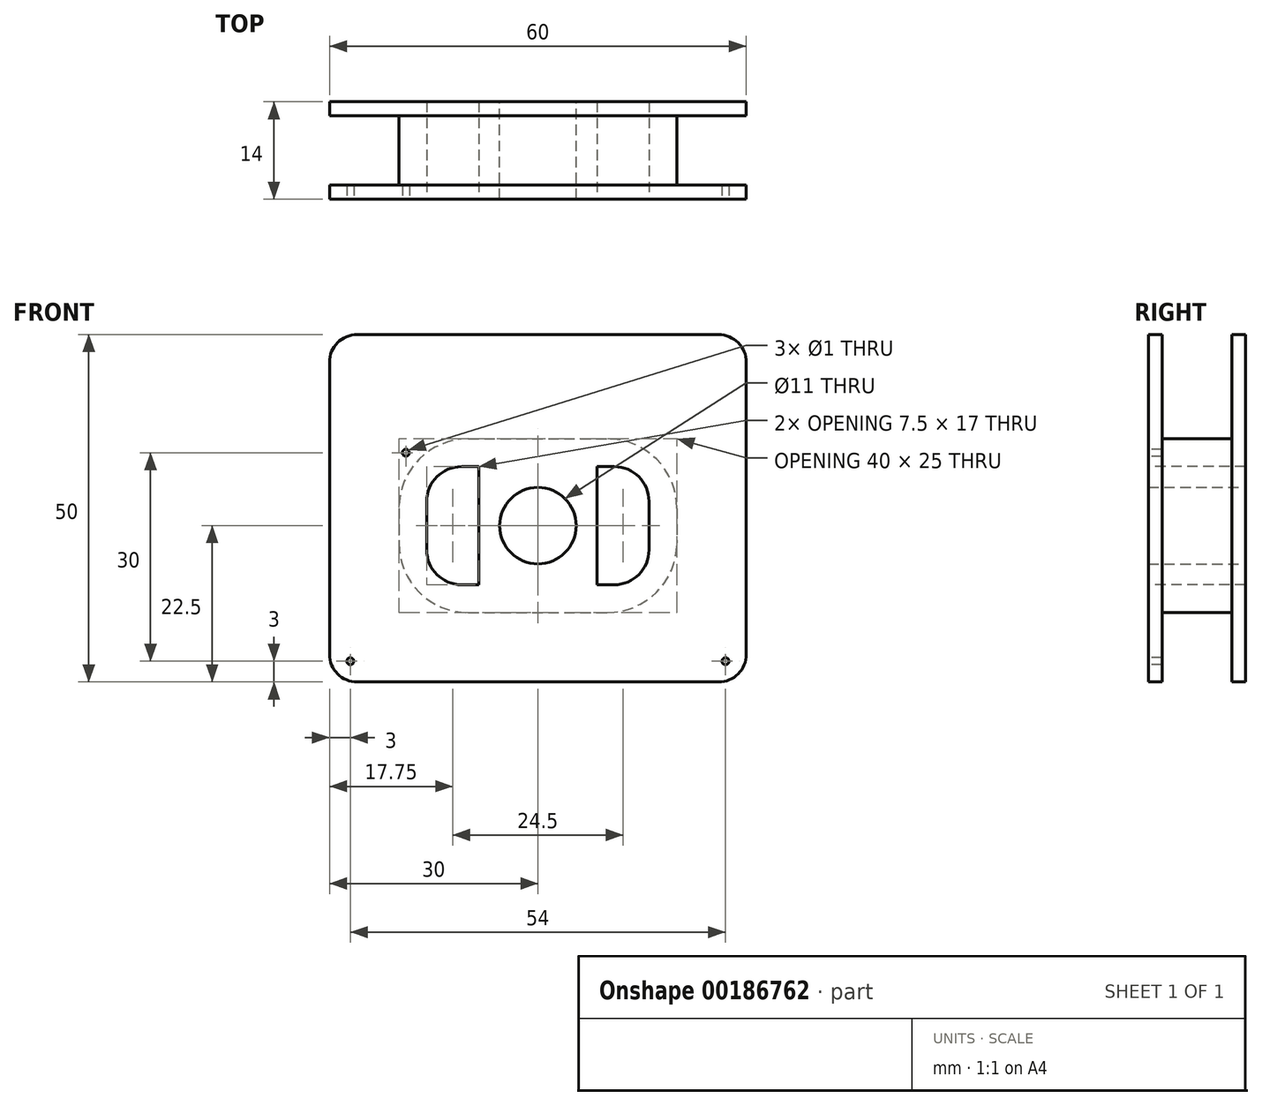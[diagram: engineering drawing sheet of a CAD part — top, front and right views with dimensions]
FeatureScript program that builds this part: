
annotation { "Feature Type Name" : "Feature", "Feature Type Description" : "" }
export const myFeature = defineFeature(function(context is Context, id is Id, definition is map)
    precondition{}
    {
        {
            var Q0;
            Q0=qCreatedBy(makeId("Front.planeOp"),FACE);
            var sketch = newSketch(context, id + "F0", { "sketchPlane" : qUnion([Q0])});
            skLineSegment(sketch, "E0.bottom", {"start": v(30, -22.5) * mm, "end": v(-30, -22.5) * mm});
            skLineSegment(sketch, "E0.top", {"start": v(30, 27.5) * mm, "end": v(-30, 27.5) * mm});
            skLineSegment(sketch, "E0.left", {"start": v(30, -22.5) * mm, "end": v(30, 27.5) * mm});
            skLineSegment(sketch, "E0.right", {"start": v(-30, -22.5) * mm, "end": v(-30, 27.5) * mm});
            skCircle(sketch, "E1", {"center": v(0, 0) * mm, "radius": 5.5 * mm});
            skSolve(sketch);
        }
        {
            var Q0;
            Q0=qSketchRegion(id+"F0",true);
            extrude(context, id + "F1", {"entities" : qUnion([Q0]), "depth" : 2 * mm});
        }
        {
            var Q0;
            Q0=makeQuery(id+"F1.opExtrude","CAP_FACE",FACE,{"disambiguationData":[OSD([sQuery(id+"F0.wireOp",EDGE,"E0.bottom"),sQuery(id+"F0.wireOp",EDGE,"E0.top"),sQuery(id+"F0.wireOp",EDGE,"E0.left"),sQuery(id+"F0.wireOp",EDGE,"E0.right"),sQuery(id+"F0.wireOp",EDGE,"E1")])],"isStart":false});
            var sketch = newSketch(context, id + "F2", { "sketchPlane" : qUnion([Q0])});
            skLineSegment(sketch, "E2.bottom", {"start": v(-20, 12.5) * mm, "end": v(20, 12.5) * mm});
            skLineSegment(sketch, "E2.top", {"start": v(-20, -12.5) * mm, "end": v(20, -12.5) * mm});
            skLineSegment(sketch, "E2.left", {"start": v(-20, 12.5) * mm, "end": v(-20, -12.5) * mm});
            skLineSegment(sketch, "E2.right", {"start": v(20, 12.5) * mm, "end": v(20, -12.5) * mm});
            skPoint(sketch, "E2.middle", {"position": v(0, 0) * mm});
            skCircle(sketch, "E3", {"center": v(0, 0) * mm, "radius": 5.5 * mm});
            skSolve(sketch);
        }
        {
            var Q0;
            Q0=qSketchRegion(id+"F2",true);
            extrude(context, id + "F3", {"entities" : qUnion([Q0]), "operationType" : NewBodyOperationType.ADD, "depth" : 10 * mm});
        }
        {
            var Q0;
            Q0=makeQuery(id+"F3.opExtrude","SWEPT_EDGE",EDGE,{"disambiguationData":[OSD([sQuery(id+"F2.wireOp",EDGE,"E2.bottom"),sQuery(id+"F2.wireOp",EDGE,"E2.right")])]});
            var Q1;
            Q1=makeQuery(id+"F3.opExtrude","SWEPT_EDGE",EDGE,{"disambiguationData":[OSD([sQuery(id+"F2.wireOp",EDGE,"E2.top"),sQuery(id+"F2.wireOp",EDGE,"E2.right")])]});
            var Q2;
            Q2=makeQuery(id+"F3.opExtrude","SWEPT_EDGE",EDGE,{"disambiguationData":[OSD([sQuery(id+"F2.wireOp",EDGE,"E2.top"),sQuery(id+"F2.wireOp",EDGE,"E2.left")])]});
            var Q3;
            Q3=makeQuery(id+"F3.opExtrude","SWEPT_EDGE",EDGE,{"disambiguationData":[OSD([sQuery(id+"F2.wireOp",EDGE,"E2.bottom"),sQuery(id+"F2.wireOp",EDGE,"E2.left")])]});
            fillet(context, id + "F4", {"entities" : qUnion([Q0, Q1, Q2, Q3]), "radius" : 10 * mm, "tangentPropagation" : true, "allowEdgeOverflow" : false});
        }
        {
            var Q0;
            Q0=makeQuery(id+"F3.opExtrude","CAP_FACE",FACE,{"disambiguationData":[OSD([sQuery(id+"F2.wireOp",EDGE,"E2.bottom"),sQuery(id+"F2.wireOp",EDGE,"E2.top"),sQuery(id+"F2.wireOp",EDGE,"E2.left"),sQuery(id+"F2.wireOp",EDGE,"E2.right"),sQuery(id+"F2.wireOp",EDGE,"E3")])],"isStart":false});
            var sketch = newSketch(context, id + "F5", { "sketchPlane" : qUnion([Q0])});
            skLineSegment(sketch, "E4.bottom", {"start": v(-30, -22.5) * mm, "end": v(30, -22.5) * mm});
            skLineSegment(sketch, "E4.top", {"start": v(-30, 27.5) * mm, "end": v(30, 27.5) * mm});
            skLineSegment(sketch, "E4.left", {"start": v(-30, -22.5) * mm, "end": v(-30, 27.5) * mm});
            skLineSegment(sketch, "E4.right", {"start": v(30, -22.5) * mm, "end": v(30, 27.5) * mm});
            skCircle(sketch, "E5", {"center": v(0, 0) * mm, "radius": 5.5 * mm});
            skSolve(sketch);
        }
        {
            var Q0;
            Q0=qSketchRegion(id+"F5",true);
            extrude(context, id + "F6", {"entities" : qUnion([Q0]), "operationType" : NewBodyOperationType.ADD, "depth" : 2 * mm});
        }
        {
            var Q0;
            Q0=makeQuery(id+"F6.opExtrude","SWEPT_EDGE",EDGE,{"disambiguationData":[OSD([sQuery(id+"F5.wireOp",EDGE,"E4.top"),sQuery(id+"F5.wireOp",EDGE,"E4.right")])]});
            var Q1;
            Q1=makeQuery(id+"F1.opExtrude","SWEPT_EDGE",EDGE,{"disambiguationData":[OSD([sQuery(id+"F0.wireOp",EDGE,"E0.top"),sQuery(id+"F0.wireOp",EDGE,"E0.left")])]});
            var Q2;
            Q2=makeQuery(id+"F6.opExtrude","SWEPT_EDGE",EDGE,{"disambiguationData":[OSD([sQuery(id+"F5.wireOp",EDGE,"E4.bottom"),sQuery(id+"F5.wireOp",EDGE,"E4.right")])]});
            var Q3;
            Q3=makeQuery(id+"F1.opExtrude","SWEPT_EDGE",EDGE,{"disambiguationData":[OSD([sQuery(id+"F0.wireOp",EDGE,"E0.bottom"),sQuery(id+"F0.wireOp",EDGE,"E0.left")])]});
            var Q4;
            Q4=makeQuery(id+"F6.opExtrude","SWEPT_EDGE",EDGE,{"disambiguationData":[OSD([sQuery(id+"F5.wireOp",EDGE,"E4.bottom"),sQuery(id+"F5.wireOp",EDGE,"E4.left")])]});
            var Q5;
            Q5=makeQuery(id+"F1.opExtrude","SWEPT_EDGE",EDGE,{"disambiguationData":[OSD([sQuery(id+"F0.wireOp",EDGE,"E0.bottom"),sQuery(id+"F0.wireOp",EDGE,"E0.right")])]});
            var Q6;
            Q6=makeQuery(id+"F6.opExtrude","SWEPT_EDGE",EDGE,{"disambiguationData":[OSD([sQuery(id+"F5.wireOp",EDGE,"E4.top"),sQuery(id+"F5.wireOp",EDGE,"E4.left")])]});
            var Q7;
            Q7=makeQuery(id+"F1.opExtrude","SWEPT_EDGE",EDGE,{"disambiguationData":[OSD([sQuery(id+"F0.wireOp",EDGE,"E0.top"),sQuery(id+"F0.wireOp",EDGE,"E0.right")])]});
            fillet(context, id + "F7", {"entities" : qUnion([Q0, Q1, Q2, Q3, Q4, Q5, Q6, Q7]), "radius" : 4 * mm, "tangentPropagation" : true, "allowEdgeOverflow" : false});
        }
        {
            var Q0;
            Q0=makeQuery(id+"F6.opExtrude","CAP_FACE",FACE,{"disambiguationData":[OSD([sQuery(id+"F5.wireOp",EDGE,"E4.bottom"),sQuery(id+"F5.wireOp",EDGE,"E4.top"),sQuery(id+"F5.wireOp",EDGE,"E4.left"),sQuery(id+"F5.wireOp",EDGE,"E4.right"),sQuery(id+"F5.wireOp",EDGE,"E5")])],"isStart":false});
            var sketch = newSketch(context, id + "F8", { "sketchPlane" : qUnion([Q0])});
            skCircle(sketch, "E6", {"center": v(-19, 10.5) * mm, "radius": 0.75 * mm});
            skCircle(sketch, "E7", {"center": v(-27, -19.5) * mm, "radius": 0.75 * mm});
            skCircle(sketch, "E8", {"center": v(27, -19.5) * mm, "radius": 0.75 * mm});
            skSolve(sketch);
        }
        {
            var Q0;
            Q0=sQuery(id+"F8.wireOp",VERTEX,"E6.center");
            var Q1;
            Q1=sQuery(id+"F8.wireOp",VERTEX,"E7.center");
            var Q2;
            Q2=sQuery(id+"F8.wireOp",VERTEX,"E8.center");
            var Q3;
            Q3=makeQuery(id+"F1.opExtrude","SWEPT_BODY",BODY,{"disambiguationData":[OSD([sQuery(id+"F0.wireOp",EDGE,"E0.bottom"),sQuery(id+"F0.wireOp",EDGE,"E0.top"),sQuery(id+"F0.wireOp",EDGE,"E0.left"),sQuery(id+"F0.wireOp",EDGE,"E0.right"),sQuery(id+"F0.wireOp",EDGE,"E1")])]});
            hole(context, id + "F9", {"style" : HoleStyle.SIMPLE, "endStyle" : HoleEndStyle.BLIND, "holeDiameter" : 1 * mm, "holeDepth" : 3 * mm, "tappedDepth" : 17.75 * mm, "tapClearance" : 3, "startFromSketch" : true, "locations" : qUnion([Q0, Q1, Q2]), "scope" : qUnion([Q3])});
        }
        {
            var Q0;
            Q0=makeQuery(id+"F6.opExtrude","CAP_FACE",FACE,{"disambiguationData":[OSD([sQuery(id+"F5.wireOp",EDGE,"E4.bottom"),sQuery(id+"F5.wireOp",EDGE,"E4.top"),sQuery(id+"F5.wireOp",EDGE,"E4.left"),sQuery(id+"F5.wireOp",EDGE,"E4.right"),sQuery(id+"F5.wireOp",EDGE,"E5")])],"isStart":false});
            var sketch = newSketch(context, id + "F10", { "sketchPlane" : qUnion([Q0])});
            skLineSegment(sketch, "E9.bottom", {"start": v(-20, 12.5) * mm, "end": v(20, 12.5) * mm});
            skLineSegment(sketch, "E9.top", {"start": v(-20, -12.5) * mm, "end": v(20, -12.5) * mm});
            skLineSegment(sketch, "E9.left", {"start": v(-20, 12.5) * mm, "end": v(-20, -12.5) * mm});
            skLineSegment(sketch, "E9.right", {"start": v(20, 12.5) * mm, "end": v(20, -12.5) * mm});
            skPoint(sketch, "E9.middle", {"position": v(0, 0) * mm});
            skLineSegment(sketch, "E10.bottom", {"start": v(16, 8.5) * mm, "end": v(8.5, 8.5) * mm});
            skLineSegment(sketch, "E10.top", {"start": v(16, -8.5) * mm, "end": v(8.5, -8.5) * mm});
            skLineSegment(sketch, "E10.left", {"start": v(16, 8.5) * mm, "end": v(16, -8.5) * mm});
            skLineSegment(sketch, "E10.right", {"start": v(8.5, 8.5) * mm, "end": v(8.5, -8.5) * mm});
            skLineSegment(sketch, "E11.bottom", {"start": v(-16, 8.5) * mm, "end": v(-8.5, 8.5) * mm});
            skLineSegment(sketch, "E11.top", {"start": v(-16, -8.5) * mm, "end": v(-8.5, -8.5) * mm});
            skLineSegment(sketch, "E11.left", {"start": v(-16, 8.5) * mm, "end": v(-16, -8.5) * mm});
            skLineSegment(sketch, "E11.right", {"start": v(-8.5, 8.5) * mm, "end": v(-8.5, -8.5) * mm});
            skSolve(sketch);
        }
        {
            var Q0;
            Q0=makeQuery(id+"F10.imprint","IMPRINT",FACE,{"disambiguationData":[TD([[makeQuery(id+"F10.imprint","IMPRINT",EDGE,{"derivedFrom":sQuery(id+"F10.wireOp",EDGE,"E11.bottom")}),-1.0]])]});
            var Q1;
            Q1=makeQuery(id+"F10.imprint","IMPRINT",FACE,{"disambiguationData":[TD([[makeQuery(id+"F10.imprint","IMPRINT",EDGE,{"derivedFrom":sQuery(id+"F10.wireOp",EDGE,"E10.bottom")}),1.0]])]});
            var Q2;
            Q2=makeQuery(id+"F10.imprint","IMPRINT",FACE,{"disambiguationData":[TD([[makeQuery(id+"F10.imprint","IMPRINT",EDGE,{"derivedFrom":sQuery(id+"F10.wireOp",EDGE,"JKNo4UeC-h3MG-pKbr-OqbK-I85fyhi2NlzQ.bottom")}),-1.0]])]});
            var Q3;
            Q3=makeQuery(id+"F10.imprint","IMPRINT",FACE,{"disambiguationData":[TD([[makeQuery(id+"F10.imprint","IMPRINT",EDGE,{"derivedFrom":sQuery(id+"F10.wireOp",EDGE,"ZiP49HXI-nA70-fZII-mEtF-8d3XIcfwj2B7.bottom")}),-1.0]])]});
            extrude(context, id + "F11", {"entities" : qUnion([Q0, Q1, Q2, Q3]), "operationType" : NewBodyOperationType.REMOVE, "oppositeDirection" : true, "depth" : 25 * mm});
        }
        {
            var Q0;
            Q0=makeQuery(id+"F11.boolean.opBoolean","COPY",EDGE,{"derivedFrom":makeQuery(id+"F11.opExtrude","SWEPT_EDGE",EDGE,{"disambiguationData":[OSD([sQuery(id+"F10.wireOp",EDGE,"E10.top"),sQuery(id+"F10.wireOp",EDGE,"E10.left")])]})});
            var Q1;
            Q1=makeQuery(id+"F11.boolean.opBoolean","COPY",EDGE,{"derivedFrom":makeQuery(id+"F11.opExtrude","SWEPT_EDGE",EDGE,{"disambiguationData":[OSD([sQuery(id+"F10.wireOp",EDGE,"E10.bottom"),sQuery(id+"F10.wireOp",EDGE,"E10.left")])]})});
            var Q2;
            Q2=makeQuery(id+"F11.boolean.opBoolean","COPY",EDGE,{"derivedFrom":makeQuery(id+"F11.opExtrude","SWEPT_EDGE",EDGE,{"disambiguationData":[OSD([sQuery(id+"F10.wireOp",EDGE,"E11.bottom"),sQuery(id+"F10.wireOp",EDGE,"E11.left")])]})});
            var Q3;
            Q3=makeQuery(id+"F11.boolean.opBoolean","COPY",EDGE,{"derivedFrom":makeQuery(id+"F11.opExtrude","SWEPT_EDGE",EDGE,{"disambiguationData":[OSD([sQuery(id+"F10.wireOp",EDGE,"E11.top"),sQuery(id+"F10.wireOp",EDGE,"E11.left")])]})});
            fillet(context, id + "F12", {"entities" : qUnion([Q0, Q1, Q2, Q3]), "radius" : 5 * mm, "tangentPropagation" : true, "allowEdgeOverflow" : false});
        }
    });
